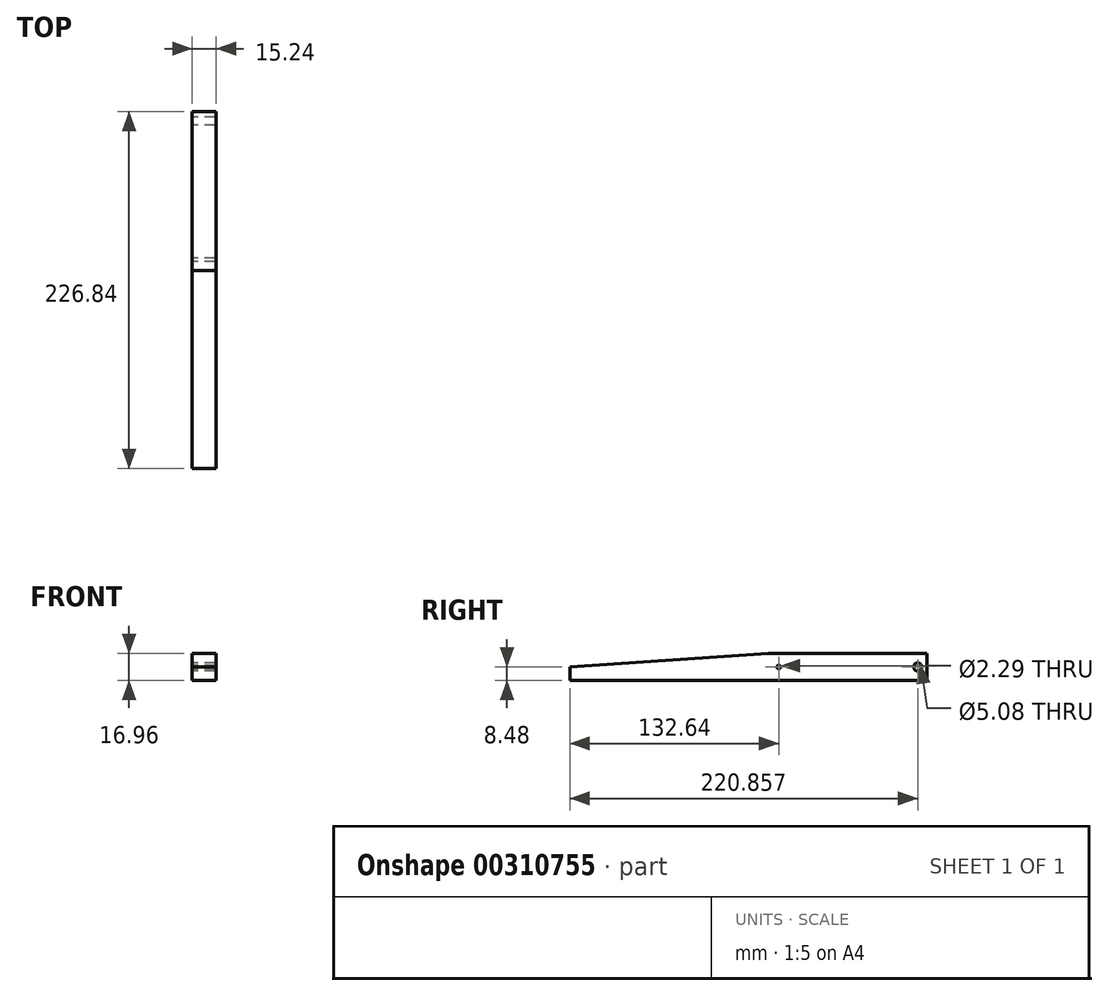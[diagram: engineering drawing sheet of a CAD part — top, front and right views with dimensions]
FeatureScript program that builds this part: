
annotation { "Feature Type Name" : "Feature", "Feature Type Description" : "" }
export const myFeature = defineFeature(function(context is Context, id is Id, definition is map)
    precondition{}
    {
        {
            var Q0;
            Q0=qCreatedBy(makeId("Right.planeOp"),FACE);
            var sketch = newSketch(context, id + "F0", { "sketchPlane" : qUnion([Q0])});
            skLineSegment(sketch, "E0", {"start": v(-64.62, -8.48) * mm, "end": v(162.22, -8.48) * mm});
            skLineSegment(sketch, "E1", {"start": v(162.22, -8.48) * mm, "end": v(162.22, 8.48) * mm});
            skLineSegment(sketch, "E2", {"start": v(162.22, 8.48) * mm, "end": v(61.35, 8.48) * mm});
            skLineSegment(sketch, "E3", {"start": v(-64.62, -8.48) * mm, "end": v(-64.62, 0) * mm});
            skLineSegment(sketch, "E4", {"start": v(61.35, 8.48) * mm, "end": v(-64.62, 0) * mm});
            skPoint(sketch, "E5", {"position": v(156.24, 0) * mm});
            skPoint(sketch, "E5.positionSnap0", {"position": v(162.22, 0) * mm});
            skPoint(sketch, "E6", {"position": v(68.02, 0) * mm});
            skLineSegment(sketch, "E7", {"start": v(24.18, 5.98) * mm, "end": v(24.18, -8.48) * mm});
            skLineSegment(sketch, "E8", {"start": v(20.55, 5.73) * mm, "end": v(20.55, -8.48) * mm});
            skLineSegment(sketch, "E9", {"start": v(60.85, 8.48) * mm, "end": v(60.85, -8.48) * mm});
            skLineSegment(sketch, "E10", {"start": v(73.92, 8.48) * mm, "end": v(73.92, 2.58) * mm});
            skLineSegment(sketch, "E11", {"start": v(73.92, -8.48) * mm, "end": v(73.92, -2.21) * mm});
            skLineSegment(sketch, "E12", {"start": v(73.92, 2.58) * mm, "end": v(148.4, 2.58) * mm});
            skLineSegment(sketch, "E13", {"start": v(73.92, -2.21) * mm, "end": v(148.4, -2.21) * mm});
            skLineSegment(sketch, "E14", {"start": v(148.4, -2.21) * mm, "end": v(148.4, -8.48) * mm});
            skLineSegment(sketch, "E15", {"start": v(148.4, 2.58) * mm, "end": v(148.4, 8.48) * mm});
            skLineSegment(sketch, "E16", {"start": v(-13.84, -8.48) * mm, "end": v(-13.84, 3.42) * mm});
            skLineSegment(sketch, "E17", {"start": v(-9.98, -8.48) * mm, "end": v(-9.98, 3.68) * mm});
            skLineSegment(sketch, "E18", {"start": v(-54.08, 0.7) * mm, "end": v(-54.08, -8.48) * mm});
            skLineSegment(sketch, "E19", {"start": v(-54.08, -8.48) * mm, "end": v(-64.62, -8.48) * mm});
            skLineSegment(sketch, "E20", {"start": v(-64.62, 0) * mm, "end": v(-54.08, 0.7) * mm});
            skSolve(sketch);
        }
        {
            var Q0;
            Q0=makeQuery(id+"F0.imprint","IMPRINT",FACE,{"disambiguationData":[TD([[makeQuery(id+"F0.imprint","IMPRINT",EDGE,{"derivedFrom":sQuery(id+"F0.wireOp",EDGE,"E0")}),1.0]])]});
            extrude(context, id + "F1", {"entities" : qUnion([Q0]), "depth" : 15.24 * mm});
        }
        {
            var Q0;
            Q0=sQuery(id+"F0.wireOp",VERTEX,"E6");
            var Q1;
            Q1=makeQuery(id+"F1.opExtrude","SWEPT_BODY",BODY,{"disambiguationData":[OSD([sQuery(id+"F0.wireOp",EDGE,"E0"),sQuery(id+"F0.wireOp",EDGE,"E1"),sQuery(id+"F0.wireOp",EDGE,"E2"),sQuery(id+"F0.wireOp",EDGE,"E3"),sQuery(id+"F0.wireOp",EDGE,"E4")])]});
            hole(context, id + "F2", {"style" : HoleStyle.SIMPLE, "endStyle" : HoleEndStyle.BLIND, "oppositeDirection" : true, "holeDiameter" : 2.3 * mm, "holeDepth" : 15.24 * mm, "tappedDepth" : 12.7 * mm, "tapClearance" : 3, "startFromSketch" : true, "locations" : qUnion([Q0]), "scope" : qUnion([Q1])});
        }
        {
            var Q0;
            Q0=sQuery(id+"F0.wireOp",VERTEX,"E5");
            var Q1;
            Q1=makeQuery(id+"F1.opExtrude","SWEPT_BODY",BODY,{"disambiguationData":[OSD([sQuery(id+"F0.wireOp",EDGE,"E0"),sQuery(id+"F0.wireOp",EDGE,"E1"),sQuery(id+"F0.wireOp",EDGE,"E2"),sQuery(id+"F0.wireOp",EDGE,"E9"),sQuery(id+"F0.wireOp",EDGE,"E10"),sQuery(id+"F0.wireOp",EDGE,"E11"),sQuery(id+"F0.wireOp",EDGE,"E12"),sQuery(id+"F0.wireOp",EDGE,"E13"),sQuery(id+"F0.wireOp",EDGE,"E14"),sQuery(id+"F0.wireOp",EDGE,"E15")])]});
            hole(context, id + "F3", {"style" : HoleStyle.SIMPLE, "endStyle" : HoleEndStyle.BLIND, "oppositeDirection" : true, "holeDiameter" : 5.08 * mm, "holeDepth" : 15.24 * mm, "tappedDepth" : 12.7 * mm, "tapClearance" : 3, "startFromSketch" : true, "locations" : qUnion([Q0]), "scope" : qUnion([Q1])});
        }
        {
            var Q0;
            Q0=makeQuery(id+"F0.imprint","IMPRINT",FACE,{"disambiguationData":[TD([[makeQuery(id+"F0.imprint","IMPRINT",EDGE,{"derivedFrom":sQuery(id+"F0.wireOp",EDGE,"E18")}),-1.0]])]});
            var Q1;
            {var subQ2=sQuery(id+"F0.wireOp",EDGE,"E16");Q1=makeQuery(id+"F0.imprint","IMPRINT",FACE,{"disambiguationData":[TD([[makeQuery(id+"F0.imprint","IMPRINT",EDGE,{"derivedFrom":subQ2}),1.0]])]});}
            var Q2;
            {var subQ0=sQuery(id+"F0.wireOp",EDGE,"E16");Q2=makeQuery(id+"F0.imprint","IMPRINT",FACE,{"disambiguationData":[TD([[makeQuery(id+"F0.imprint","IMPRINT",EDGE,{"derivedFrom":subQ0}),-1.0]])]});}
            var Q3;
            {var subQ0=sQuery(id+"F0.wireOp",EDGE,"E8");Q3=makeQuery(id+"F0.imprint","IMPRINT",FACE,{"disambiguationData":[TD([[makeQuery(id+"F0.imprint","IMPRINT",EDGE,{"derivedFrom":subQ0}),-1.0]])]});}
            var Q4;
            {var subQ0=sQuery(id+"F0.wireOp",EDGE,"E7");Q4=makeQuery(id+"F0.imprint","IMPRINT",FACE,{"disambiguationData":[TD([[makeQuery(id+"F0.imprint","IMPRINT",EDGE,{"derivedFrom":subQ0}),1.0]])]});}
            var Q5;
            {var subQ0=sQuery(id+"F0.wireOp",EDGE,"E7");Q5=makeQuery(id+"F0.imprint","IMPRINT",FACE,{"disambiguationData":[TD([[makeQuery(id+"F0.imprint","IMPRINT",EDGE,{"derivedFrom":subQ0}),-1.0]])]});}
            extrude(context, id + "F4", {"entities" : qUnion([Q0, Q1, Q2, Q3, Q4, Q5]), "operationType" : NewBodyOperationType.ADD, "depth" : 15.24 * mm});
        }
        {
            var Q0;
            {var subQ0=sQuery(id+"F0.wireOp",EDGE,"E11");Q0=makeQuery(id+"F0.imprint","IMPRINT",FACE,{"disambiguationData":[TD([[makeQuery(id+"F0.imprint","IMPRINT",EDGE,{"derivedFrom":subQ0}),-1.0]])]});}
            var Q1;
            {var subQ0=sQuery(id+"F0.wireOp",EDGE,"E10");Q1=makeQuery(id+"F0.imprint","IMPRINT",FACE,{"disambiguationData":[TD([[makeQuery(id+"F0.imprint","IMPRINT",EDGE,{"derivedFrom":subQ0}),1.0]])]});}
            extrude(context, id + "F5", {"entities" : qUnion([Q0, Q1]), "operationType" : NewBodyOperationType.ADD, "depth" : 15.24 * mm});
        }
    });
